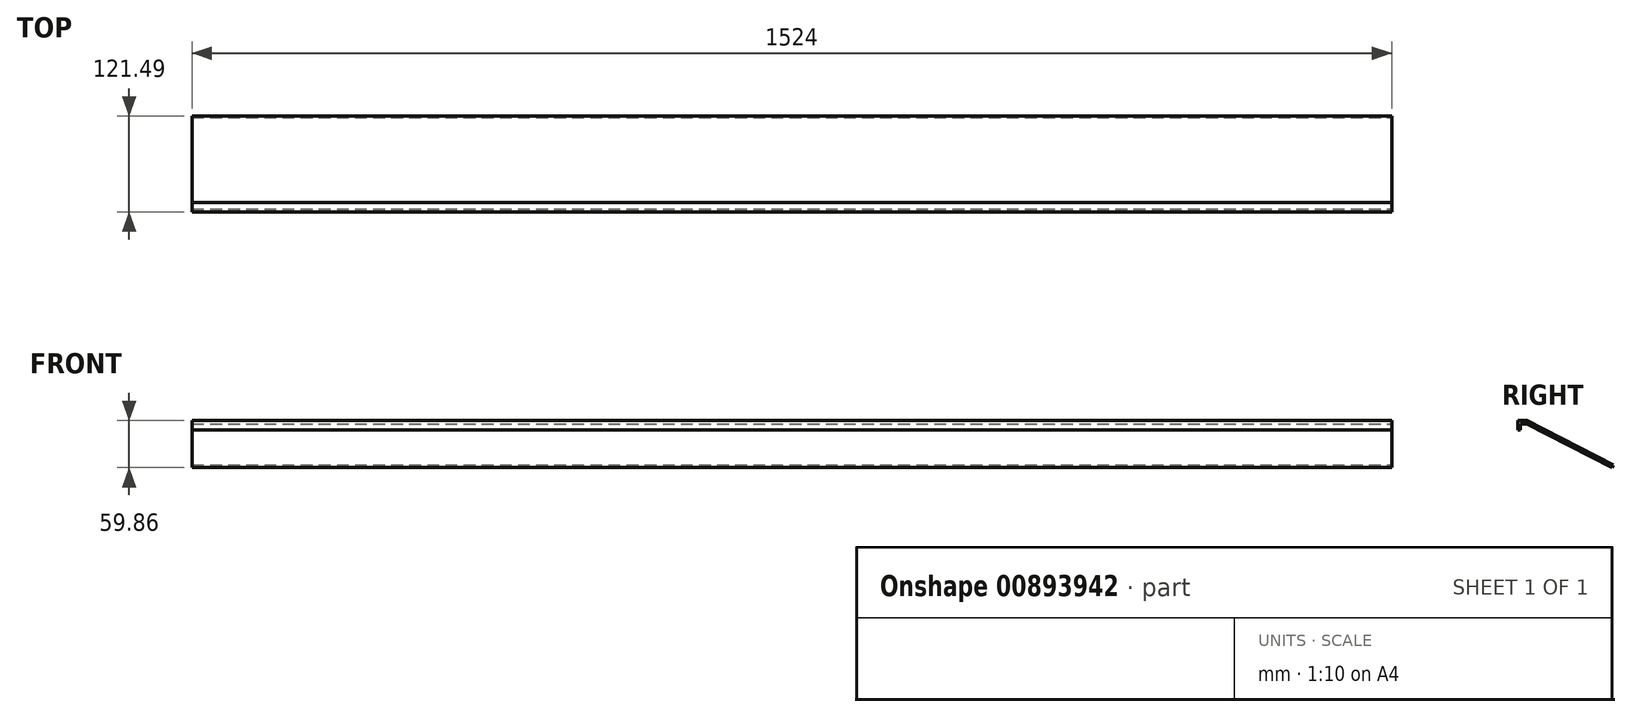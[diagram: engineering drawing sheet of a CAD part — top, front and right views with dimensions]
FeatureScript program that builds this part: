
annotation { "Feature Type Name" : "Feature", "Feature Type Description" : "" }
export const myFeature = defineFeature(function(context is Context, id is Id, definition is map)
    precondition{}
    {
        {
            var Q0;
            Q0=qCreatedBy(makeId("Right.planeOp"),FACE);
            var sketch = newSketch(context, id + "F0", { "sketchPlane" : qUnion([Q0])});
            skLineSegment(sketch, "E0", {"start": v(-44.13, 32.73) * mm, "end": v(-44.13, 44.72) * mm});
            skLineSegment(sketch, "E1", {"start": v(-44.13, 44.72) * mm, "end": v(-32.34, 44.72) * mm});
            skLineSegment(sketch, "E2", {"start": v(-32.34, 44.72) * mm, "end": v(77.36, -11.7) * mm});
            skLineSegment(sketch, "E3", {"start": v(77.36, -11.7) * mm, "end": v(75.59, -15.14) * mm});
            skLineSegment(sketch, "E4", {"start": v(75.59, -15.14) * mm, "end": v(-32.67, 40.54) * mm});
            skLineSegment(sketch, "E5", {"start": v(-32.67, 40.54) * mm, "end": v(-40.6, 40.54) * mm});
            skLineSegment(sketch, "E6", {"start": v(-40.6, 40.54) * mm, "end": v(-40.6, 32.73) * mm});
            skLineSegment(sketch, "E7", {"start": v(-40.6, 32.73) * mm, "end": v(-44.13, 32.73) * mm});
            skSolve(sketch);
        }
        {
            var Q0;
            Q0 = qSketchRegion(id + "F0", true);
            extrude(context, id + "F1", {"entities" : qUnion([Q0]), "oppositeDirection" : true, "depth" : 1524 * mm, "offsetDistance" : 25.4 * mm});
        }
    });
